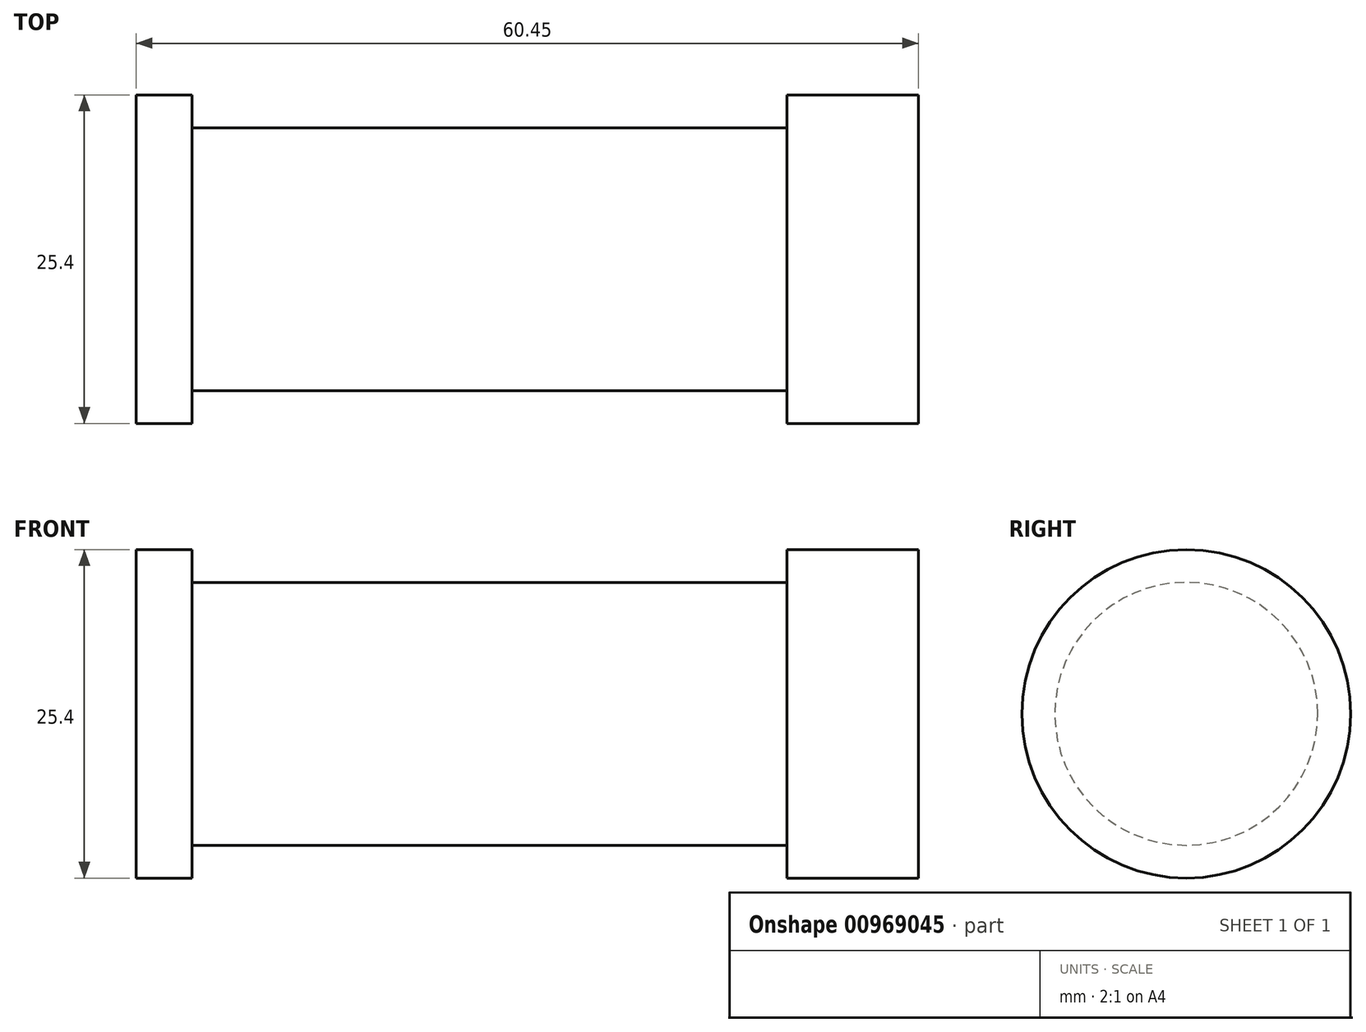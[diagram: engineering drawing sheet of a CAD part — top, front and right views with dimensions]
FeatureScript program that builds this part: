
annotation { "Feature Type Name" : "Feature", "Feature Type Description" : "" }
export const myFeature = defineFeature(function(context is Context, id is Id, definition is map)
    precondition{}
    {
        {
            var Q0;
            Q0=qCreatedBy(makeId("Front.planeOp"),FACE);
            var sketch = newSketch(context, id + "F0", { "sketchPlane" : qUnion([Q0])});
            skLineSegment(sketch, "E0", {"start": v(0, 0) * mm, "end": v(0, 12.7) * mm});
            skLineSegment(sketch, "E1", {"start": v(0, 12.7) * mm, "end": v(10.16, 12.7) * mm});
            skLineSegment(sketch, "E2", {"start": v(10.16, 12.7) * mm, "end": v(10.16, 10.16) * mm});
            skLineSegment(sketch, "E3", {"start": v(10.16, 10.16) * mm, "end": v(56.13, 10.16) * mm});
            skLineSegment(sketch, "E4", {"start": v(56.13, 10.16) * mm, "end": v(56.13, 12.7) * mm});
            skLineSegment(sketch, "E5", {"start": v(56.13, 12.7) * mm, "end": v(66.3, 12.7) * mm});
            skLineSegment(sketch, "E6", {"start": v(66.3, 12.7) * mm, "end": v(66.3, 0) * mm});
            skLineSegment(sketch, "E7", {"start": v(66.3, 0) * mm, "end": v(0, 0) * mm});
            skLineSegment(sketch, "E8", {"start": v(5.84, 15.24) * mm, "end": v(-0.5, 15.24) * mm});
            skLineSegment(sketch, "E9", {"start": v(-0.5, 15.24) * mm, "end": v(-10.88, 3.85) * mm});
            skLineSegment(sketch, "E10", {"start": v(0, 0) * mm, "end": v(-6.65, 0) * mm});
            skCircle(sketch, "E11", {"center": v(-6.65, 0) * mm, "radius": 5.72 * mm});
            skCircle(sketch, "E12", {"center": v(-6.65, 0) * mm, "radius": 3.18 * mm});
            skLineSegment(sketch, "E13", {"start": v(5.84, 15.24) * mm, "end": v(5.84, -9.4) * mm});
            skLineSegment(sketch, "E14", {"start": v(5.84, -9.4) * mm, "end": v(-8.18, -5.5) * mm});
            skSolve(sketch);
        }
        {
            var Q0;
            {var subQ0=sQuery(id+"F0.wireOp",EDGE,"E2");Q0=makeQuery(id+"F0.imprint","IMPRINT",FACE,{"disambiguationData":[TD([[makeQuery(id+"F0.imprint","IMPRINT",EDGE,{"derivedFrom":subQ0}),-1.0]])]});}
            var Q1;
            Q1=sQuery(id+"F0.wireOp",EDGE,"E7");
            revolve(context, id + "F1", {"surfaceOperationType" : NewSurfaceOperationType.NEW, "entities" : qUnion([Q0]), "axis" : qUnion([Q1]), "revolveType" : RevolveType.FULL});
        }
    });
